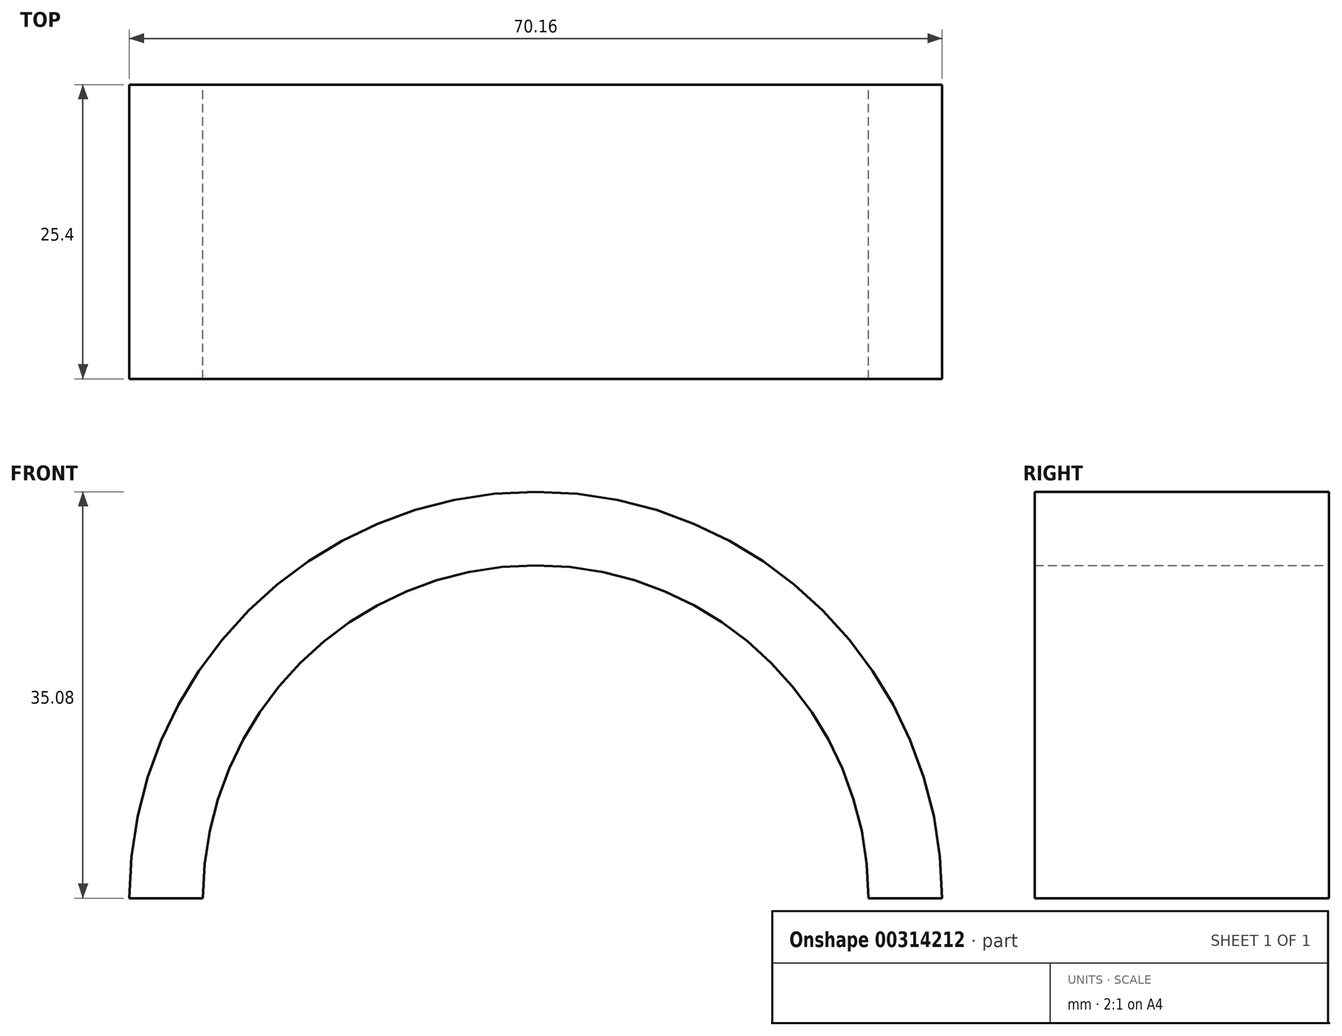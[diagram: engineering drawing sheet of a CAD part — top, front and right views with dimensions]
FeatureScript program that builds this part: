
annotation { "Feature Type Name" : "Feature", "Feature Type Description" : "" }
export const myFeature = defineFeature(function(context is Context, id is Id, definition is map)
    precondition{}
    {
        {
            var Q0;
            Q0=qCreatedBy(makeId("Front.planeOp"),FACE);
            var sketch = newSketch(context, id + "F0", { "sketchPlane" : qUnion([Q0])});
            skArc(sketch, "E0", {"start": v(28.73, 0) * mm, "mid": v(0, 28.73) * mm, "end": v(-28.73, 0) * mm});
            skArc(sketch, "E1.0", {"start": v(35.08, 0) * mm, "mid": v(0, 35.08) * mm, "end": v(-35.08, 0) * mm});
            skLineSegment(sketch, "E2", {"start": v(35.08, 0) * mm, "end": v(28.73, 0) * mm});
            skLineSegment(sketch, "E3", {"start": v(-35.08, 0) * mm, "end": v(-28.73, 0) * mm});
            skSolve(sketch);
        }
        {
            var Q0;
            Q0 = qSketchRegion(id + "F0", true);
            extrude(context, id + "F1", {"entities" : qUnion([Q0]), "depth" : 25.4 * mm});
        }
    });
